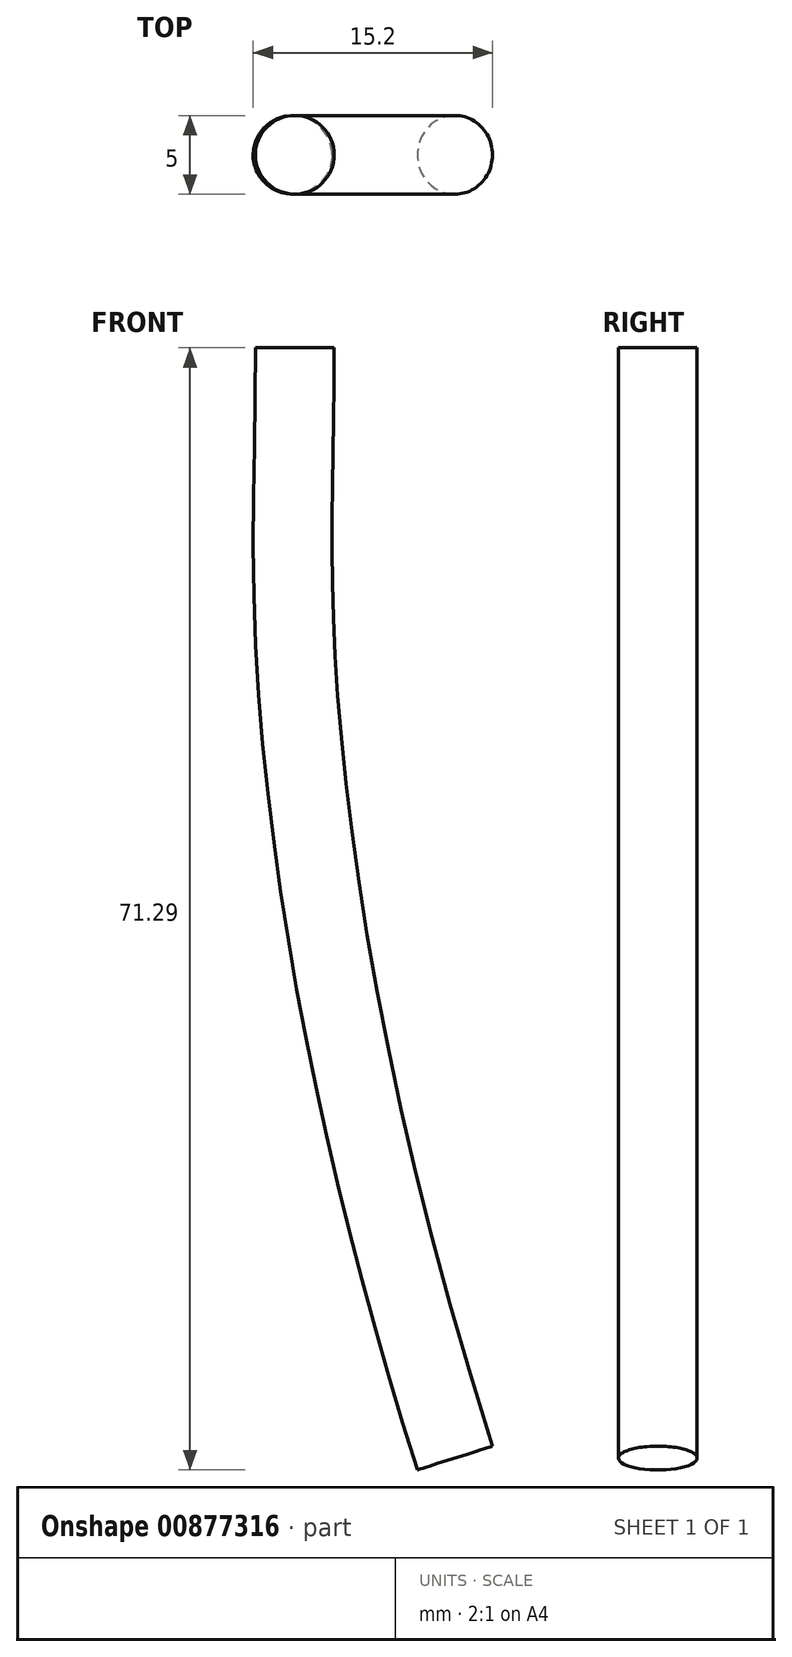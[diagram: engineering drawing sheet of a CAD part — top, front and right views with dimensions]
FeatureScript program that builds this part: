
annotation { "Feature Type Name" : "Feature", "Feature Type Description" : "" }
export const myFeature = defineFeature(function(context is Context, id is Id, definition is map)
    precondition{}
    {
        {
            var Q0;
            Q0=qCreatedBy(makeId("Top.planeOp"),FACE);
            var sketch = newSketch(context, id + "F0", { "sketchPlane" : qUnion([Q0])});
            skCircle(sketch, "E0", {"center": v(0, 0) * mm, "radius": 2.5 * mm});
            skSolve(sketch);
        }
        {
            var Q0;
            Q0=qCreatedBy(makeId("Front.planeOp"),FACE);
            var sketch = newSketch(context, id + "F1", { "sketchPlane" : qUnion([Q0])});
            skFitSpline(sketch, "E1", {"points": [v(0, 0) * mm, v(0, -18.6) * mm, v(10.17, -70.53) * mm], "startDerivative": vector(0, -55.36) * mm, "endDerivative": vector(34.15, -107.62) * mm});
            skSolve(sketch);
        }
        {
            var Q0;
            Q0 = qSketchRegion(id + "F0", true);
            var Q1;
            Q1=sQuery(id+"F1.wireOp",EDGE,"E1");
            sweep(context, id + "F2", {"profiles" : qUnion([Q0]), "path" : qUnion([Q1])});
        }
    });
